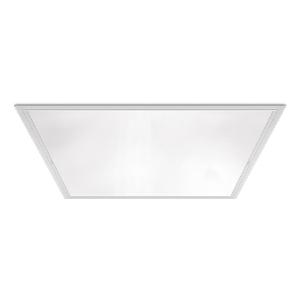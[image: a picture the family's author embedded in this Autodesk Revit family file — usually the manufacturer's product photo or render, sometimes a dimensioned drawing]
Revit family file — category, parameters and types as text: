
# Revit family: 3f_filippi_-_l_340_luce_diffusa_lgs_3f_filippi_-_23857_-_l_340_25w-840_lgs_596x596
name_source: partatom
category: Lighting Fixtures
units: mm (PartAtom-declared; Revit-internal decimal feet)

## family parameters
Cut with Voids When Loaded = No
Host = Face
Light Source = No
Part Type = Normal
Room Calculation Point = No
Round Connector Dimension = Use Diameter
Shared = No

## types (1)
- 3F Filippi - L 340 Luce Diffusa LGS (1 x LED, 3785 lm, 29 W, 4000 K)
    Apparent Load = 29 VA
    Approval mark = ENEC
    CIE Flux Codes = 67 92 98 100 100
    Color Rendering = 80
    Color Temperature = 4000 K
    Control Gear = Electronic ballast
    Default Elevation = 1800 mm
    Description = ILLUMINOTECHNICAL
Luminous efficiency 100% (DLOR 100%, ULOR 0%).
Initial luminous flux of the luminaire 3785 lm.
Direct symmetric distribution.
Installation Interdistance Transv.D = 1.19 x hu - Long.D = 1.17 x hu.
Average luminance <1500 cd/m² for radial angles >65°.
Tabular UGR (CIE 117 - 4H-8H; S=0.25H; 70/50/20): RUG 16.4 - 16.4.
Beam angle: 87° - 86°.
Luminous efficacy 131 lm/W.
Lifetime (L93/B10): 30000 h. (tq+25°C)
Lifetime (L90/B10): 50000 h. (tq+25°C)
Lifetime (L85/B10): 80000 h. (tq+25°C)
Lifetime (L80/B10): 100000 h. (tq+25°C)
Sudden decreased luminous flux after 50000 hours: 0% (C0).
Photobiological safety in compliance with IEC/TR 62778: RG0 risk exempt, (IEC 62471).
In compliance with IEC/EN 62722-2-1 - IEC/EN 62717 standards.

SOURCE
Squared LED module 25W/840.
Energy efficiency class (UE 2019/2020 - UE 2019/2015): C.
CIE 13.3 Colour rendering index: CRI >80 (R9 <50%).
IES TM-30 Fidelity Index: Rf = 84 Rg = 95.
CCT nominal colour temperature 4000 K.
Colour initial tolerance (MacAdam): SDCM 3.

MECHANICAL
Housing in hot-galvanised steel, painted in white polyester.
Perimetral frame in white polycarbonate.
LGS micro-prismatic flat diffuser in transparent methacrylate (PMMA), multi-lenticular exterior, anti-glare.
Anti-glare opal polycarbonate filter for brightness uniformity.
Luminaire with limited surface temperature. - D - (EN 60598-2-24)
Dimensions: 596x596 mm, height 80 mm. Weight 4.4 kg.
IP40 protection degree.
Mechanical strength to impacts IK06 (1 joule).
Glow-wire test resistance 650°C.

ELECTRICAL
Wiring on a separate unit.
Halogen Free electronic wiring 230V-50/60Hz, power factor 0.95, THD <25%, constant output current, SELV, class II, 1 driver.
Power of the luminaire 29 W.
CE - IEC 60598-1 - EN 60598-1.
SAFE FLICKER: PstLM=<1 and SVM=<0.4 (IEC TR 61547-1 and IEC TR 63158), to ensure a more comfortable and safe light.
Luminaire compliant with EN 60598-2-22 for power supply from a centralised emergency system CPSS (Central Power Supply System), not incorporated in the luminaire - high risk areas excluded. The default power and flux are 100% in AC and 100% in DC.
Ambient temperature from 0°C to +40°C.
Temperature class T6 max 85°C.
Relative humidity UR: <85%.

INSTALLATION
Lay-on or pull-up recessed fitting using frame accessory.
All accessories dedicated to this product are available on the Catalog and on our website www.3F-Filippi.com.

APPLICATIONS
Suitable product for food production plants (HACCP), IFS (Food Version 6), BRC (GSFS Food Version 7).
Environments: with VDTs, meeting rooms, offices.
Environments: architectural, commercial, staterooms, banks.
Environments where demanding visual tasks are performed and soft diffuse light is required for optimal visual comfort and total shielding of the light source.

WARNING
Luminaire designed for disposal/recycling at end-of-life.
Replaceable (LED only) light source by a professional. Replaceable control gear by a professional.
    Height = 0 mm  [stored 0 ft]
    Lamp = 1 x LED
    Lamp Light Flux = 3785 lm
    Lamp Power = 29 W
    Lamp count = 1
    Length = 596 mm
    Lifetime = 50000 h
    Luminous efficacy = 131 lm/W
    Manufacturer = 3F Filippi
    ModVariant = No
    Model = 3F Filippi - 23857 - L 340 25W-840 LGS 596x596
    Mounting Place = Ceiling
    Mounting Type = Recessed
    Number of Poles = 1
    OnlyDefault = Yes
    Power Factor = 1
    Product Name = 3F Filippi - L 340 Luce Diffusa LGS
    Product group = recessed luminaire
    ProductGroupID = 4
    Protection Class = Protection class II
    Protection Degree = IP 40
    RLX_Detail_Level = 1
    RLX_Emergency_Light_Flux = 0 lm
    RLX_Emergency_Type = 0
    RLX_Emergency_Type_DB = No
    RlxData = <blob elided: 153441 chars, md5=586a6979>
    Socket = socket
    Standby Power = 0 W
    System Light Flux = 3785 lm
    System Power = 29 W
    Type Comments = Product without accessories
    Type Image = 3ffilippi_l_340_luce_diffusa_lgs.jpg
    URL = http://relux.com
    VarID = ---
    Voltage = 0 V
    Weight = 0.00 kg
    Width = 596 mm

note: [stored X ft] marks values corroborated as IEEE doubles in the binary element streams (Revit-internal decimal feet)

## geometry (parser evidence)
native form markers: Blend x4, Sweep x11
no freeform markers — native parametric forms only
